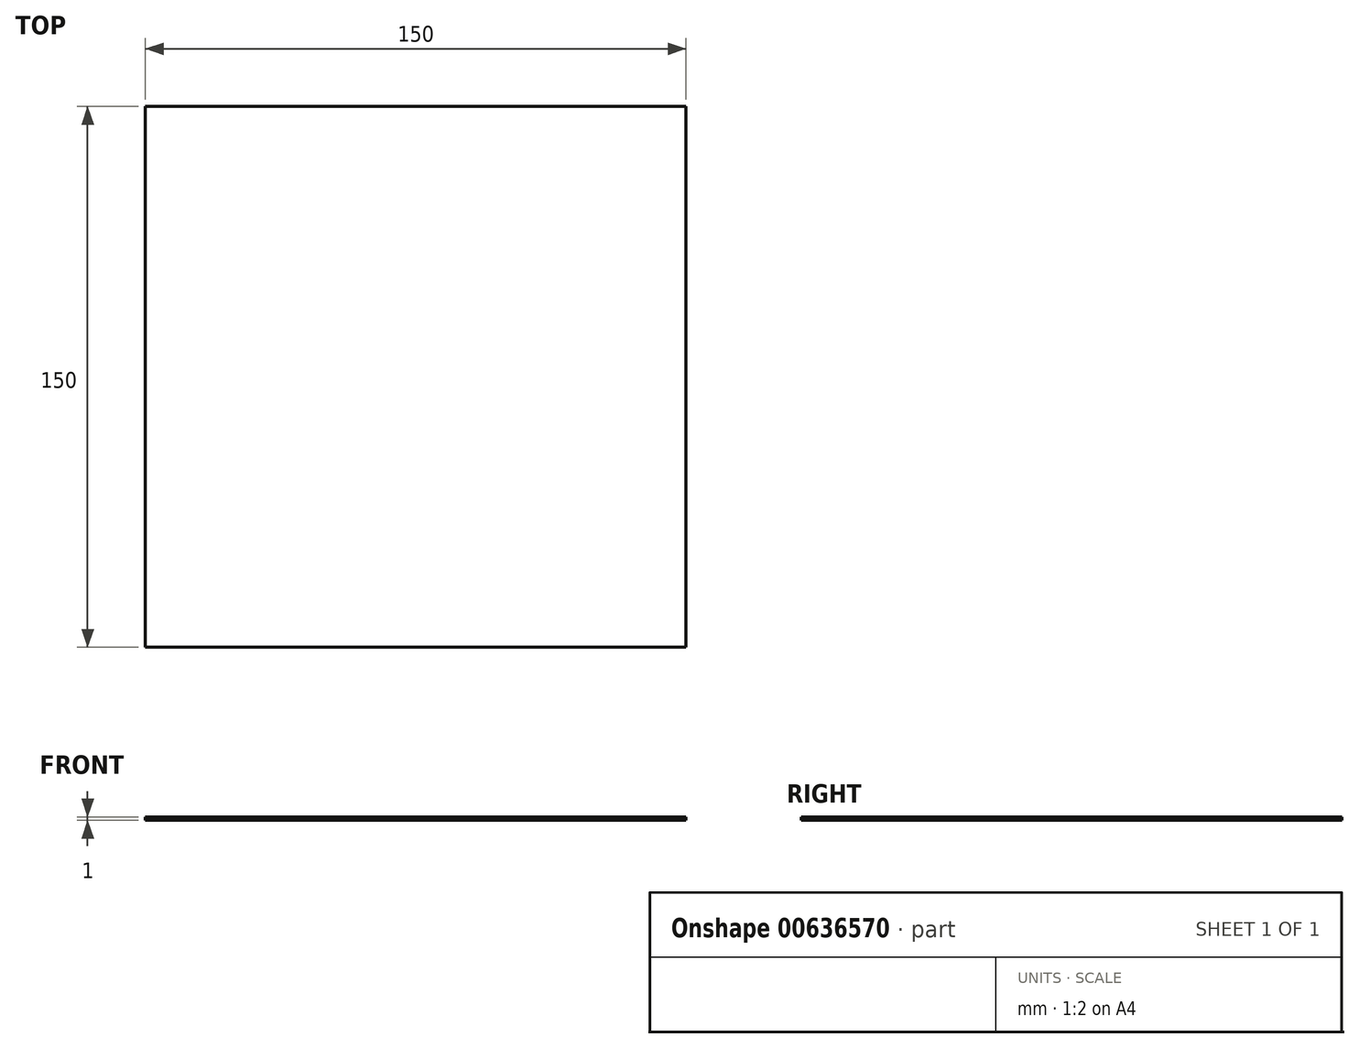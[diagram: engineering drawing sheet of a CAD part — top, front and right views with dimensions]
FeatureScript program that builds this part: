
annotation { "Feature Type Name" : "Feature", "Feature Type Description" : "" }
export const myFeature = defineFeature(function(context is Context, id is Id, definition is map)
    precondition{}
    {
        {
            var Q0;
            Q0=qCreatedBy(makeId("Top.planeOp"), FACE);
            var sketch = newSketch(context, id + "F0", { "sketchPlane" : qUnion([Q0])});
            skLineSegment(sketch, "E0.bottom", {"start": v(75, -75) * mm, "end": v(-75, -75) * mm});
            skLineSegment(sketch, "E0.top", {"start": v(75, 75) * mm, "end": v(-75, 75) * mm});
            skLineSegment(sketch, "E0.left", {"start": v(75, -75) * mm, "end": v(75, 75) * mm});
            skLineSegment(sketch, "E0.right", {"start": v(-75, -75) * mm, "end": v(-75, 75) * mm});
            skPoint(sketch, "E0.middle", {"position": v(0, 0) * mm});
            skSolve(sketch);
        }
        {
            var Q0;
            Q0 = qSketchRegion(id + "F0", true);
            extrude(context, id + "F1", {"entities" : qUnion([Q0]), "depth" : 1 * mm, "offsetDistance" : 25 * mm});
        }
    });
